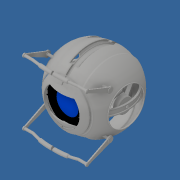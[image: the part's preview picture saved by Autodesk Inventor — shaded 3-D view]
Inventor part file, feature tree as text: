
AUTODESK INVENTOR PART (.ipt)
format: ipt  version: 2018.3 (Build 223284000, 284)  size: 2,169,856 bytes
history: native  units: in
note: dims shown in document units (in); Inventor stores cm internally (conversion verified against a paired STEP export)
features: sketch x33, extrude x21, plane x10, other x9, chamfer x8, mirror x7, pattern_circular x4, fillet x3, revolve x2, sweep x2, projected_geometry x1
ambient origin geometry x8: Origin, YZ Plane, XZ Plane, XY Plane, X Axis, Y Axis, Z Axis, Center Point
bodies: Solid1 (feature_tree)
feature tree (100):
  other  "Wheatly 2.ipt"
  extrude  "Extrusion1"  Depth=2.75in
  extrude  "Extrusion3"  Depth=0.25in TaperAngle=0.0deg
  mirror  "Mirror1"
  extrude  "Extrusion4"  Depth=0.15in TaperAngle=0.0deg
  plane  "Work Plane1"
  extrude  "Extrusion5"  Depth=0.75in TaperAngle=0.0deg
  extrude  "Extrusion6"  Depth=2.5in
  sketch  "Sketch8"  dims[d18=0.25in d19=0.0in d20=2.3in]
  extrude  "Extrusion7"  Depth=2.3in
  extrude  "Extrusion8"  Depth=0.5375in TaperAngle=0.0deg
  extrude  "Extrusion9"  Depth=0.05in TaperAngle=0.0deg
  plane  "Work Plane2"
  extrude  "Extrusion10"  Depth=3.3in
  chamfer  "Chamfer1"  Distance=0.1in
  chamfer  "Chamfer2"  Distance=0.25in
  sketch  "Sketch13"  dims[d32=2.6in]
  pattern_circular  "Circular Pattern1"  Count=3 Angle=360.0deg
  pattern_circular  "Circular Pattern4"  Count=6 Angle=360.0deg
  chamfer  "Chamfer4"  Distance=0.25in
  chamfer  "Chamfer5"  Distance=0.25in
  chamfer  "Chamfer6"  Distance=0.25in
  chamfer  "Chamfer7"  Distance=0.25in
  plane  "Work Plane3"
  mirror  "Mirror2"
  pattern_circular  "Circular Pattern5"  Count=6 Angle=360.0deg
  extrude  "Extrusion11"  Depth=0.5in TaperAngle=0.0deg
  plane  "Work Plane4"
  revolve  "Revolution1"  Angle=90.0deg
  other  "Work Point4"
  plane  "Work Plane6"
  other  "Work Point5"
  other  "Work Point6"
  sketch  "Sketch16"  dims[d37=135.0deg]
  sketch  "Sketch17"  dims[d38=0.5in d39=0.25in d40=0.0in d41=0.0in]
  plane  "Work Plane7"
  mirror  "Mirror3"
  pattern_circular  "Circular Pattern6"  Count=3 Angle=360.0deg
  extrude  "Extrusion12"  Depth=0.25in
  sketch  "Sketch19"  dims[d45=0.25in d46=0.125in d47=0.1374in d48=1.1811in d49=360.0deg d60=2.3622in d61=360.0deg d63=0.25in d64=0.125in d65=0.1374in d66=0.25in d67=0.125in d68=0.1374in d69=0.25in d70=0.125in d71=0.1374in d72=0.25in d73=0.125in d74=0.1374in d75=2.3622in d76=360.0deg]
  extrude  "Extrusion13"  TaperAngle=90.0deg  [1 undecoded]
  mirror  "Mirror4"
  plane  "Work Plane8"
  plane  "Work Plane9"
  extrude  "Extrusion14"  Depth=0.2in
  extrude  "Extrusion15"  Depth=0.1in
  fillet  "Fillet1"  Radius=0.05in
  mirror  "Mirror5"
  extrude  "Extrusion16"  Depth=0.6in TaperAngle=0.0deg
  extrude  "Extrusion17"  Depth=1.1in
  extrude  "Extrusion18"  Depth=0.8in
  extrude  "Extrusion19"  Depth=0.05in TaperAngle=0.0deg
  chamfer  "Chamfer8"  Distance=0.05in
  chamfer  "Chamfer9"  Distance=0.04in
  plane  "Work Plane10"
  revolve  "Revolution2"  [1 undecoded]
  extrude  "Extrusion20"  Depth=1.9in
  extrude  "Extrusion21"  TaperAngle=90.0deg  [1 undecoded]
  extrude  "Extrusion22"  Depth=0.08in
  sketch  "Sketch31"  dims[d112=0.6in d113=0.05in d114=0.0in d115=0.05in d116=0.0in d117=0.04in d118=0.125in d119=0.1374in]
  plane  "Work Plane11"
  sweep  "Sweep1"
  sweep  "Sweep2"
  fillet  "Fillet2"  Radius=2.0in
  fillet  "Fillet3"  Radius=0.2in
  mirror  "Mirror6"
  mirror  "Mirror7"
  other  "Solid1::Wheatly 2.ipt"
  other  "TaggingFeature1"
  sketch  "Sketch2"  dims[d0=0.3937in d1=2.75in]
  sketch  "Sketch4"  dims[d2=3.3in d3=0.25in d4=0.0in]
  sketch  "Sketch5"  dims[d10=1.25in d11=0.15in d12=0.0in]
  sketch  "Sketch6"  dims[d13=3.3in d14=0.75in d15=0.0in]
  sketch  "Sketch7"  dims[d16=2.875in d17=2.5in]
  sketch  "Sketch9"  dims[d21=2.175in d22=0.5375in d23=0.0in]
  sketch  "Sketch10"  dims[d24=1.9in d25=0.05in d26=0.0in]
  sketch  "Sketch11"  dims[d27=2.3in d28=3.3in d29=0.1in d30=0.0in]
  projected_geometry  "Projected Loop3"
  sketch  "Sketch12"  dims[d31=3.2in]
  sketch  "Sketch14"  dims[d33=105.0deg d34=0.25in d35=0.0in]
  other  "Work Point1"
  other  "Work Point2"
  sketch  "Sketch15"  dims[d36=135.0deg]
  sketch  "Sketch18"  dims[d42=0.25in d43=0.125in d44=0.1374in]
  sketch  "Sketch20"  dims[d78=2.3622in d80=360.0deg d82=0.5in d83=0.0in]
  sketch  "Sketch21"  dims[d84=0.125in d85=90.0deg]
  sketch  "Sketch22"  dims[d86=90.0deg]
  sketch  "Sketch23"  dims[d87=0.03in d88=1.1811in d89=360.0deg]
  sketch  "Sketch24"  dims[d91=0.5in d92=0.0in d93=0.25in]
  sketch  "Sketch25"  dims[d94=90.0deg d95=90.0deg]
  sketch  "Sketch26"  dims[d96=0.75in d97=0.0in d98=0.2in]
  sketch  "Sketch27"  dims[d99=0.45in d100=0.0in d101=0.1in d102=0.05in d103=0.0in]
  sketch  "Sketch28"  dims[d104=1.0in d105=0.6in d106=0.0in]
  sketch  "Sketch29"  dims[d107=0.5in d108=1.1in]
  sketch  "Sketch30"  dims[d109=0.2in d110=0.0in d111=0.8in]
  other  "Work Point7"
  sketch  "Sketch32"  dims[d120=0.04in d121=0.125in d122=0.1374in d123=1.3in]
  sketch  "Sketch33"  dims[d124=0.1in d125=1.9in]
  sketch  "Sketch34"  dims[d126=0.1in d127=90.0deg]
  sketch  "Sketch35"  dims[d128=0.08in d129=0.08in d130=90.0deg d131=0.5in d132=2.0in d133=0.2in d136=0.9697in d137=0.3in d138=0.1in d139=0.0in d140=0.025in d141=0.125in d142=0.0in d143=0.0in d144=0.65in d145=0.0in d146=0.125in d147=0.125in d148=0.0in d149=0.0in d150=0.3in d151=0.0in d152=0.0in d153=0.1in d154=0.01in]
note: 3 required parameter values undecoded (feature->parameter linkage not recoverable at this tier; creation-order binding heuristic only, values carry confidence <= 0.55)